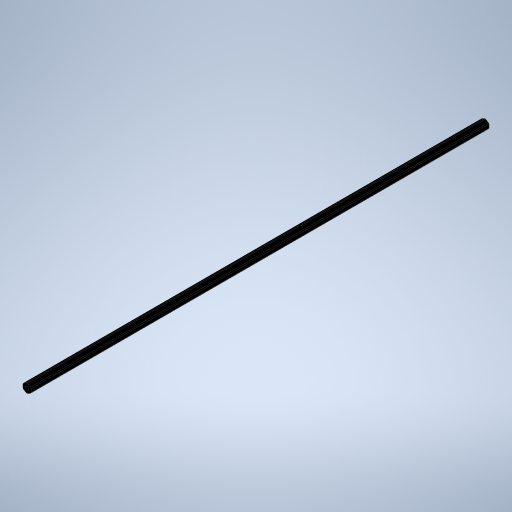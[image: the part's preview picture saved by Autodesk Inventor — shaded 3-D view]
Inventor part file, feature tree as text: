
AUTODESK INVENTOR PART (.ipt)
format: ipt  version: 2023.4 (Build 274418000, 418)  size: 272,384 bytes
history: native  units: in
note: dims shown in document units (in); Inventor stores cm internally (conversion verified against a paired STEP export)
features: extrude x2, projected_geometry x2, hole x1
ambient origin geometry x8: Origin, YZ Plane, XZ Plane, XY Plane, X Axis, Y Axis, Z Axis, Center Point
bodies: Solid1 (feature_tree)
feature tree (5):
  extrude  "Extrusion1"  TaperAngle=0.0deg  [1 undecoded]
  hole  "Hole1"  [1 undecoded]
  extrude  "Extrusion3"  TaperAngle=0.0deg  [1 undecoded]
  projected_geometry  "Project Cut Edges1"
  projected_geometry  "Project Cut Edges2"
note: 3 required parameter values undecoded (feature->parameter linkage not recoverable at this tier; creation-order binding heuristic only, values carry confidence <= 0.55)
